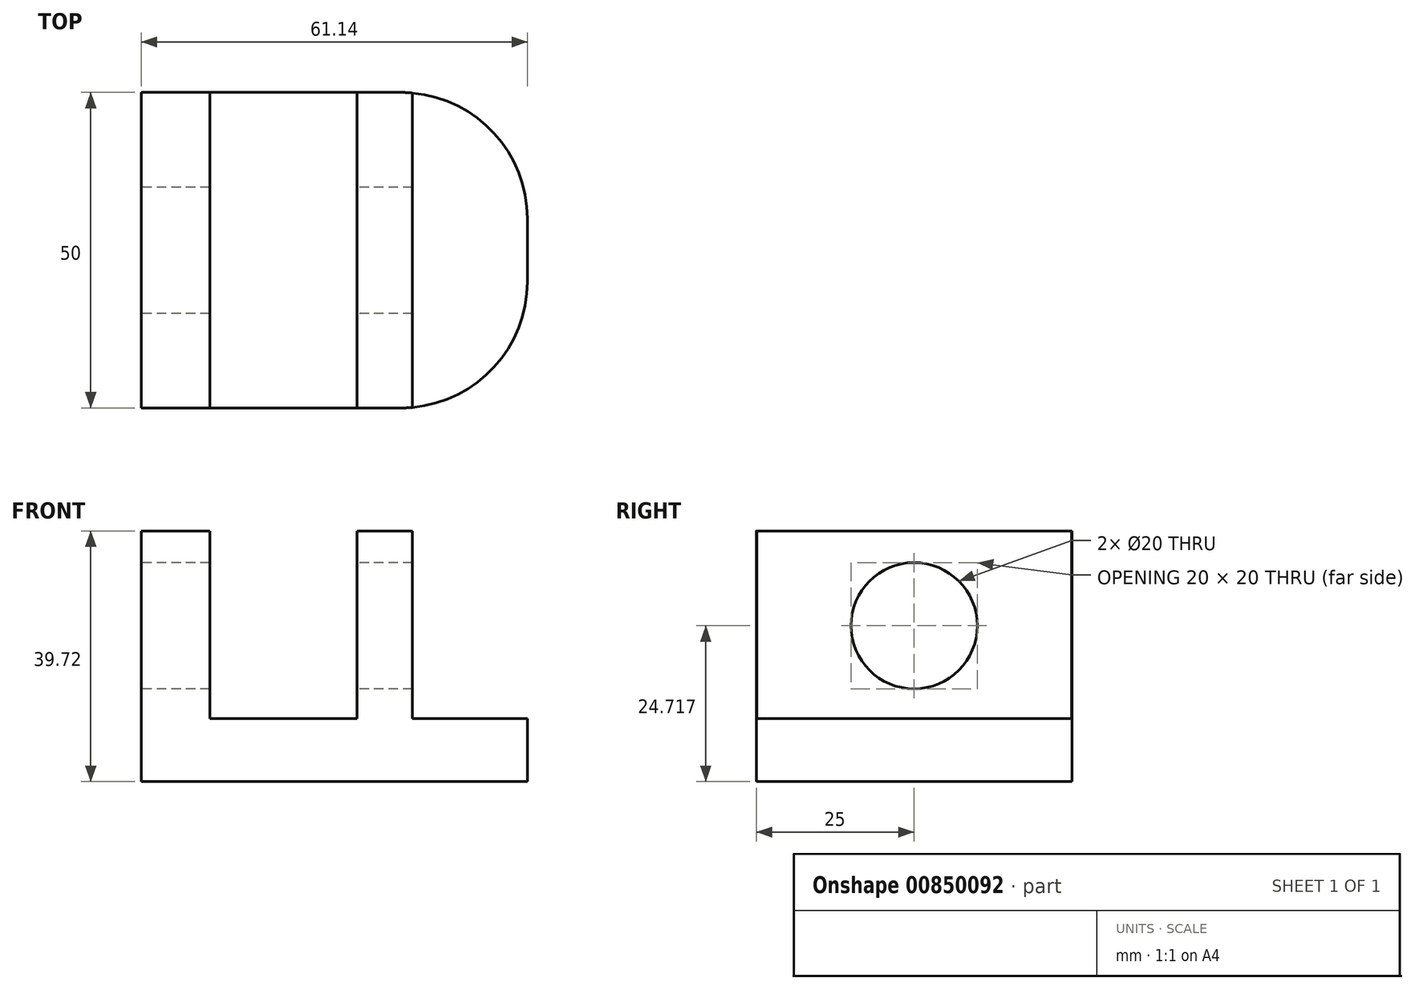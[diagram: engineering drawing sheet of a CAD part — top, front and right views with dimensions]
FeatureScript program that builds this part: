
annotation { "Feature Type Name" : "Feature", "Feature Type Description" : "" }
export const myFeature = defineFeature(function(context is Context, id is Id, definition is map)
    precondition{}
    {
        {
            var Q0;
            Q0=qCreatedBy(makeId("Front.planeOp"),FACE);
            var sketch = newSketch(context, id + "F0", { "sketchPlane" : qUnion([Q0])});
            skLineSegment(sketch, "E0", {"start": v(0, 0) * mm, "end": v(0, 39.72) * mm});
            skLineSegment(sketch, "E1", {"start": v(10.86, 39.72) * mm, "end": v(10.86, 9.98) * mm});
            skLineSegment(sketch, "E2", {"start": v(10.86, 9.98) * mm, "end": v(34.14, 9.98) * mm});
            skLineSegment(sketch, "E3", {"start": v(34.14, 9.98) * mm, "end": v(34.14, 39.72) * mm});
            skLineSegment(sketch, "E4", {"start": v(34.14, 39.72) * mm, "end": v(42.95, 39.72) * mm});
            skLineSegment(sketch, "E5", {"start": v(42.95, 39.72) * mm, "end": v(42.95, 9.98) * mm});
            skLineSegment(sketch, "E6", {"start": v(42.95, 9.98) * mm, "end": v(61.14, 9.98) * mm});
            skLineSegment(sketch, "E7", {"start": v(61.14, 9.98) * mm, "end": v(61.14, 0) * mm});
            skLineSegment(sketch, "E8", {"start": v(61.14, 0) * mm, "end": v(0, 0) * mm});
            skLineSegment(sketch, "E9", {"start": v(10.86, 39.72) * mm, "end": v(0, 39.72) * mm});
            skSolve(sketch);
        }
        {
            var Q0;
            Q0=makeQuery(id+"F0.imprint","IMPRINT",FACE,{"disambiguationData":[TD([[makeQuery(id+"F0.imprint","IMPRINT",EDGE,{"derivedFrom":sQuery(id+"F0.wireOp",EDGE,"E0")}),-1.0]])]});
            extrude(context, id + "F1", {"entities" : qUnion([Q0]), "depth" : 50 * mm, "offsetDistance" : 25 * mm});
        }
        {
            var Q0;
            Q0=makeQuery(id+"F1.opExtrude","SWEPT_FACE",FACE,{"disambiguationData":[OSD([sQuery(id+"F0.wireOp",EDGE,"E0")])]});
            var sketch = newSketch(context, id + "F2", { "sketchPlane" : qUnion([Q0])});
            skCircle(sketch, "E10", {"center": v(25, 24.72) * mm, "radius": 10 * mm});
            skSolve(sketch);
        }
        {
            var Q0;
            Q0=makeQuery(id+"F2.imprint","IMPRINT",FACE,{"disambiguationData":[TD([[makeQuery(id+"F2.imprint","IMPRINT",EDGE,{"derivedFrom":sQuery(id+"F2.wireOp",EDGE,"E10")}),1.0]])]});
            var Q1;
            Q1=sQuery(id+"F2.wireOp",EDGE,"E10");
            extrude(context, id + "F3", {"entities" : qUnion([Q0]), "operationType" : NewBodyOperationType.REMOVE, "surfaceEntities" : qUnion([Q1]), "endBound" : BoundingType.THROUGH_ALL, "oppositeDirection" : true, "depth" : 25 * mm, "offsetDistance" : 25 * mm});
        }
        {
            var Q0;
            Q0=makeQuery(id+"F1.opExtrude","CAP_EDGE",EDGE,{"disambiguationData":[OSD([sQuery(id+"F0.wireOp",EDGE,"E7")])],"isStart":true});
            var Q1;
            Q1=makeQuery(id+"F1.opExtrude","CAP_EDGE",EDGE,{"disambiguationData":[OSD([sQuery(id+"F0.wireOp",EDGE,"E7")])],"isStart":false});
            fillet(context, id + "F4", {"entities" : qUnion([Q0, Q1]), "radius" : 20 * mm, "tangentPropagation" : true, "allowEdgeOverflow" : false});
        }
    });
